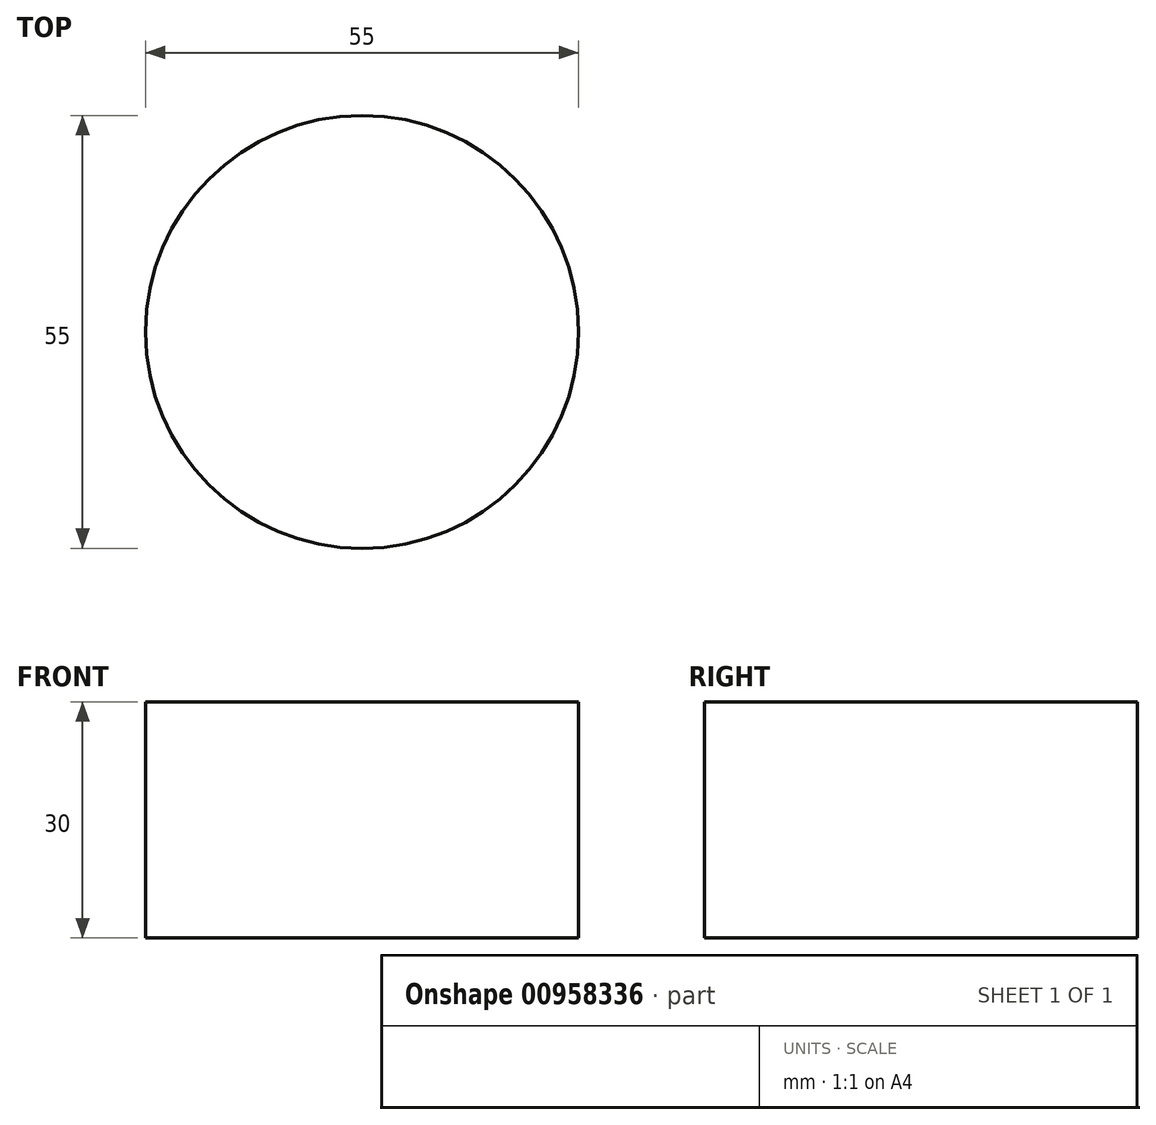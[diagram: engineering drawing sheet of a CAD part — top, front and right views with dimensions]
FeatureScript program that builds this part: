
annotation { "Feature Type Name" : "Feature", "Feature Type Description" : "" }
export const myFeature = defineFeature(function(context is Context, id is Id, definition is map)
    precondition{}
    {
        {
            var Q0;
            Q0=qCreatedBy(makeId("Top.planeOp"),FACE);
            var sketch = newSketch(context, id + "F0", { "sketchPlane" : qUnion([Q0])});
            skCircle(sketch, "E0", {"center": v(0, 0) * mm, "radius": 27.5 * mm});
            skSolve(sketch);
        }
        {
            var Q0;
            Q0=makeQuery(id+"F0.imprint","IMPRINT",FACE,{"disambiguationData":[TD([[makeQuery(id+"F0.imprint","IMPRINT",EDGE,{"derivedFrom":sQuery(id+"F0.wireOp",EDGE,"E0")}),1.0]])]});
            extrude(context, id + "F1", {"entities" : qUnion([Q0]), "depth" : 30 * mm, "offsetDistance" : 25 * mm});
        }
    });
